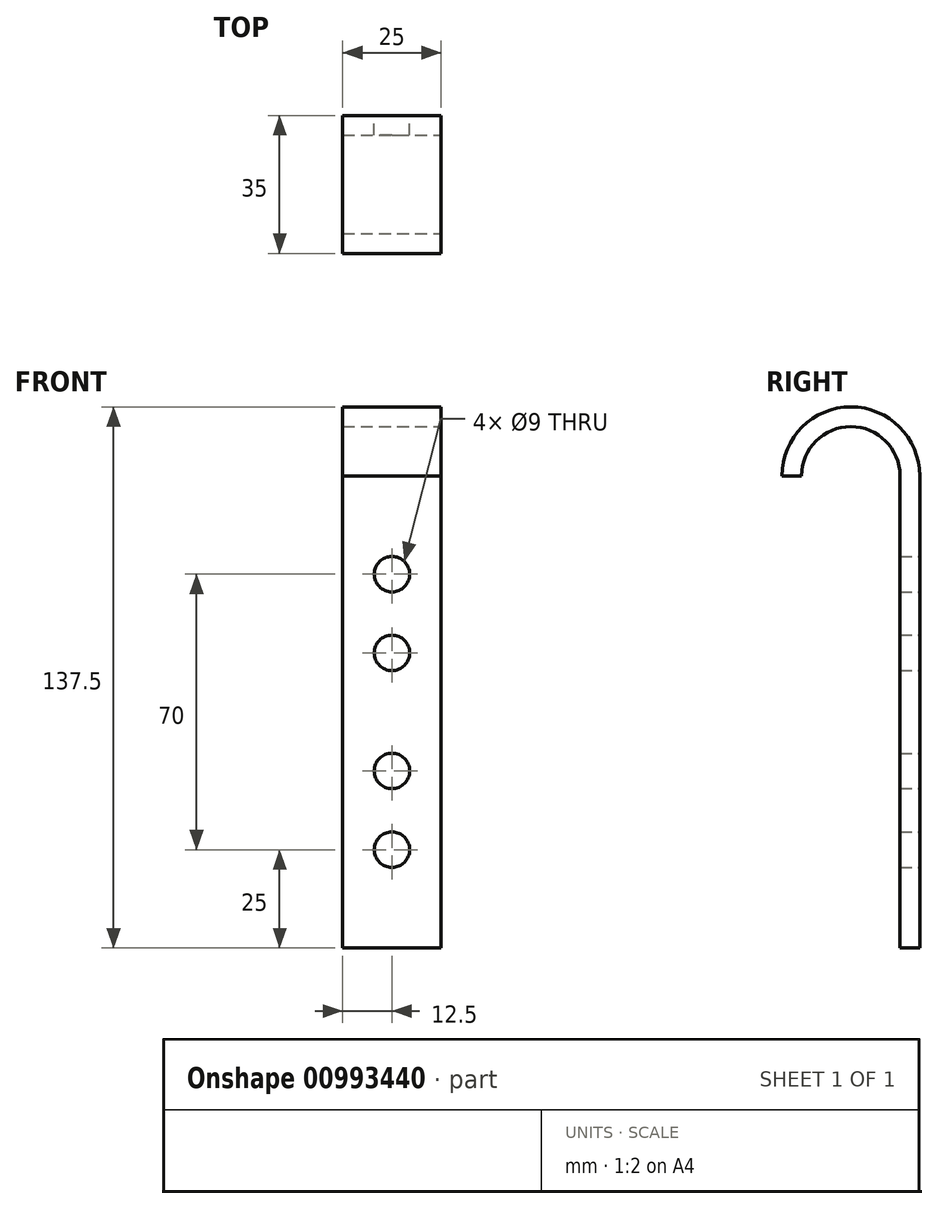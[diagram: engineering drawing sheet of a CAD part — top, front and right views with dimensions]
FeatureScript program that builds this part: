
annotation { "Feature Type Name" : "Feature", "Feature Type Description" : "" }
export const myFeature = defineFeature(function(context is Context, id is Id, definition is map)
    precondition{}
    {
        {
            var Q0;
            Q0=qCreatedBy(makeId("Right.planeOp"),FACE);
            cPlane(context, id + "F0", {"entities" : qUnion([Q0]), "cplaneType" : CPlaneType.OFFSET, "offset" : 60 * mm, "width" : 150 * mm, "height" : 150 * mm});
        }
        {
            var Q0;
            Q0=qCreatedBy(id+"F0.planeOp",FACE);
            var sketch = newSketch(context, id + "F1", { "sketchPlane" : qUnion([Q0])});
            skArc(sketch, "E0", {"start": v(12.5, 0) * mm, "mid": v(0, 12.5) * mm, "end": v(-12.5, 0) * mm});
            skArc(sketch, "E1.0", {"start": v(17.5, 0) * mm, "mid": v(0, 17.5) * mm, "end": v(-17.5, 0) * mm});
            skLineSegment(sketch, "E2", {"start": v(-17.5, 0) * mm, "end": v(-12.5, 0) * mm});
            skPoint(sketch, "E3.orphan", {"position": v(-25.7, 0) * mm});
            skLineSegment(sketch, "E4", {"start": v(12.5, 0) * mm, "end": v(12.5, -120) * mm});
            skLineSegment(sketch, "E5", {"start": v(12.5, -120) * mm, "end": v(17.5, -120) * mm});
            skLineSegment(sketch, "E6", {"start": v(17.5, -120) * mm, "end": v(17.5, 0) * mm});
            skSolve(sketch);
        }
        {
            var Q0;
            Q0 = qSketchRegion(id + "F1", true);
            extrude(context, id + "F2", {"entities" : qUnion([Q0]), "oppositeDirection" : true, "depth" : 25 * mm, "offsetDistance" : 25 * mm});
        }
        {
            var Q0;
            Q0=makeQuery(id+"F2.opExtrude","SWEPT_FACE",FACE,{"disambiguationData":[OSD([sQuery(id+"F1.wireOp",EDGE,"E6")])]});
            var sketch = newSketch(context, id + "F3", { "sketchPlane" : qUnion([Q0])});
            skPoint(sketch, "E7", {"position": v(-47.5, -25) * mm});
            skPoint(sketch, "E8", {"position": v(-47.5, -45) * mm});
            skSolve(sketch);
        }
        {
            var Q0;
            Q0=sQuery(id+"F3.wireOp",VERTEX,"E7");
            var Q1;
            Q1=sQuery(id+"F3.wireOp",VERTEX,"E8");
            var Q2;
            Q2=makeQuery(id+"F2.opExtrude","SWEPT_BODY",BODY,{"disambiguationData":[OSD([sQuery(id+"F1.wireOp",EDGE,"E0"),sQuery(id+"F1.wireOp",EDGE,"E1.0"),sQuery(id+"F1.wireOp",EDGE,"E2"),sQuery(id+"F1.wireOp",EDGE,"E4"),sQuery(id+"F1.wireOp",EDGE,"E5"),sQuery(id+"F1.wireOp",EDGE,"E6")])]});
            hole(context, id + "F4", {"style" : HoleStyle.SIMPLE, "endStyle" : HoleEndStyle.THROUGH, "standardTappedOrClearance" : lookupTablePath({ "fit" : "Normal", "standard" : "ISO", "size" : "M8", "type" : "Clearance" }), "standardBlindInLast" : lookupTablePath({ "fit" : "Normal", "standard" : "ISO", "engagement" : "75%", "pitch" : "1.25 mm", "size" : "M8", "type" : "Clearance & tapped" }), "holeDiameter" : 9 * mm, "majorDiameter" : 5 * mm, "isTappedThrough" : true, "tappedDepth" : 12 * mm, "tapClearance" : 3, "locations" : qUnion([Q0, Q1]), "scope" : qUnion([Q2])});
        }
        {
            var Q0;
            Q0=makeQuery(id+"F2.opExtrude","SWEPT_FACE",FACE,{"disambiguationData":[OSD([sQuery(id+"F1.wireOp",EDGE,"E6")])]});
            var sketch = newSketch(context, id + "F5", { "sketchPlane" : qUnion([Q0])});
            skPoint(sketch, "E9", {"position": v(-47.5, -75) * mm});
            skPoint(sketch, "E10", {"position": v(-47.5, -95) * mm});
            skSolve(sketch);
        }
        {
            var Q0;
            Q0=sQuery(id+"F5.wireOp",VERTEX,"E9");
            var Q1;
            Q1=sQuery(id+"F5.wireOp",VERTEX,"E10");
            var Q2;
            Q2=makeQuery(id+"F2.opExtrude","SWEPT_BODY",BODY,{"disambiguationData":[OSD([sQuery(id+"F1.wireOp",EDGE,"E0"),sQuery(id+"F1.wireOp",EDGE,"E1.0"),sQuery(id+"F1.wireOp",EDGE,"E2"),sQuery(id+"F1.wireOp",EDGE,"E4"),sQuery(id+"F1.wireOp",EDGE,"E5"),sQuery(id+"F1.wireOp",EDGE,"E6")])]});
            hole(context, id + "F6", {"style" : HoleStyle.SIMPLE, "endStyle" : HoleEndStyle.THROUGH, "standardTappedOrClearance" : lookupTablePath({ "fit" : "Normal", "standard" : "ISO", "size" : "M8", "type" : "Clearance" }), "standardBlindInLast" : lookupTablePath({ "fit" : "Normal", "standard" : "ISO", "engagement" : "75%", "pitch" : "1.25 mm", "size" : "M8", "type" : "Clearance & tapped" }), "holeDiameter" : 9 * mm, "majorDiameter" : 5 * mm, "isTappedThrough" : true, "tappedDepth" : 12 * mm, "tapClearance" : 3, "locations" : qUnion([Q0, Q1]), "scope" : qUnion([Q2])});
        }
    });
